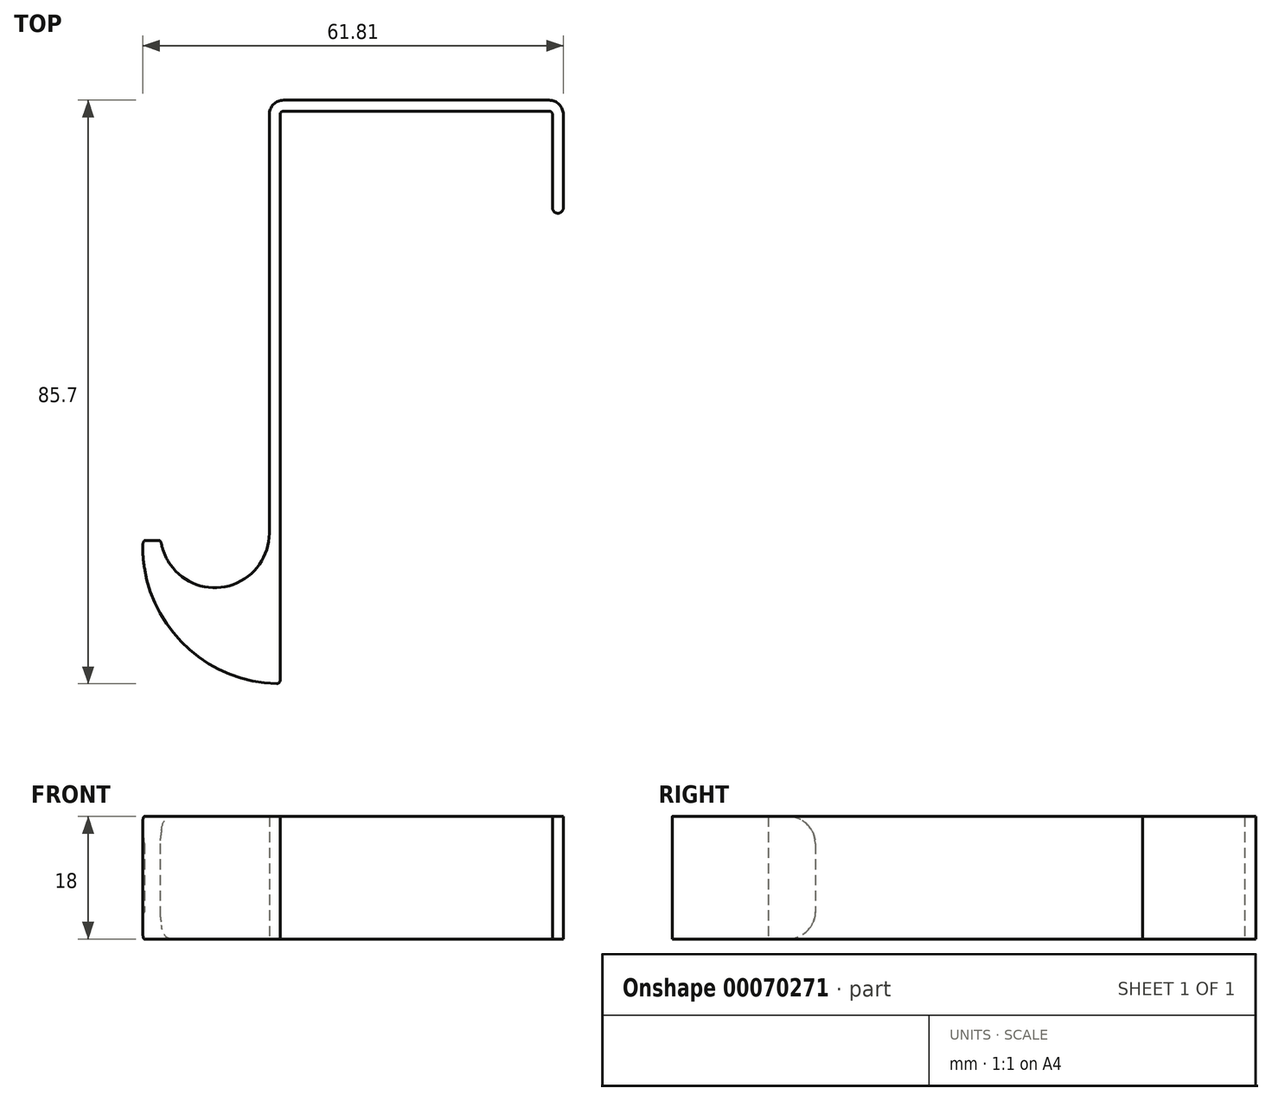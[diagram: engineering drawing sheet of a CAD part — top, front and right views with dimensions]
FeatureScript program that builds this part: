
annotation { "Feature Type Name" : "Feature", "Feature Type Description" : "" }
export const myFeature = defineFeature(function(context is Context, id is Id, definition is map)
    precondition{}
    {
        {
            var Q0;
            Q0=qCreatedBy(makeId("Top.planeOp"),FACE);
            var sketch = newSketch(context, id + "F0", { "sketchPlane" : qUnion([Q0])});
            skLineSegment(sketch, "E0", {"start": v(43.2, -15.8) * mm, "end": v(43.2, -2.1) * mm});
            skLineSegment(sketch, "E1", {"start": v(41.1, 0) * mm, "end": v(2.1, 0) * mm});
            skLineSegment(sketch, "E2", {"start": v(0, -2.1) * mm, "end": v(0, -63.6) * mm});
            skArc(sketch, "E3", {"start": v(-15.83, -65.22) * mm, "mid": v(-7.19, -71.56) * mm, "end": v(0, -63.6) * mm});
            skLineSegment(sketch, "E4", {"start": v(-15.83, -65.22) * mm, "end": v(-8, -63.6) * mm, "construction": true});
            skLineSegment(sketch, "E5", {"start": v(-8, -63.6) * mm, "end": v(0, -63.6) * mm, "construction": true});
            skArc(sketch, "E6", {"start": v(-15.83, -65.22) * mm, "mid": v(-17.35, -64.1) * mm, "end": v(-18.6, -65.5) * mm});
            skArc(sketch, "E7", {"start": v(-18.6, -65.5) * mm, "mid": v(-12.87, -79.6) * mm, "end": v(1.09, -85.7) * mm});
            skLineSegment(sketch, "E8", {"start": v(1.6, -85.2) * mm, "end": v(1.6, -2.1) * mm});
            skLineSegment(sketch, "E9", {"start": v(2.1, -1.6) * mm, "end": v(41.1, -1.6) * mm});
            skLineSegment(sketch, "E10", {"start": v(41.6, -2.1) * mm, "end": v(41.6, -15.8) * mm});
            skArc(sketch, "E11", {"start": v(41.6, -15.8) * mm, "mid": v(42.4, -16.6) * mm, "end": v(43.2, -15.8) * mm});
            skPoint(sketch, "E12.visualSharp", {"position": v(1.6, -1.6) * mm});
            skArc(sketch, "E12.filletArc", {"start": v(2.1, -1.6) * mm, "mid": v(1.75, -1.75) * mm, "end": v(1.6, -2.1) * mm});
            skPoint(sketch, "E13.visualSharp", {"position": v(41.6, -1.6) * mm});
            skArc(sketch, "E13.filletArc", {"start": v(41.6, -2.1) * mm, "mid": v(41.45, -1.75) * mm, "end": v(41.1, -1.6) * mm});
            skPoint(sketch, "E14.visualSharp", {"position": v(43.2, 0) * mm});
            skArc(sketch, "E14.filletArc", {"start": v(43.2, -2.1) * mm, "mid": v(42.58, -0.62) * mm, "end": v(41.1, 0) * mm});
            skPoint(sketch, "E15.visualSharp", {"position": v(0, 0) * mm});
            skArc(sketch, "E15.filletArc", {"start": v(2.1, 0) * mm, "mid": v(0.62, -0.62) * mm, "end": v(0, -2.1) * mm});
            skLineSegment(sketch, "E16", {"start": v(-18.6, -65.5) * mm, "end": v(-18.6, -63.6) * mm, "construction": true});
            skLineSegment(sketch, "E17", {"start": v(-18.6, -63.6) * mm, "end": v(-8, -63.6) * mm, "construction": true});
            skPoint(sketch, "E18.visualSharp", {"position": v(1.6, -85.7) * mm});
            skArc(sketch, "E18.filletArc", {"start": v(1.09, -85.7) * mm, "mid": v(1.45, -85.56) * mm, "end": v(1.6, -85.2) * mm});
            skLineSegment(sketch, "E19", {"start": v(-18.6, -64.1) * mm, "end": v(-15.83, -64.1) * mm, "construction": true});
            skLineSegment(sketch, "E20", {"start": v(-15.83, -64.1) * mm, "end": v(-15.83, -65.22) * mm, "construction": true});
            skSolve(sketch);
        }
        {
            var Q0;
            Q0=makeQuery(id+"F0.imprint","IMPRINT",FACE,{"disambiguationData":[TD([[makeQuery(id+"F0.imprint","IMPRINT",EDGE,{"derivedFrom":sQuery(id+"F0.wireOp",EDGE,"E0")}),1.0]])]});
            extrude(context, id + "F1", {"entities" : qUnion([Q0]), "endBound" : BoundingType.SYMMETRIC, "depth" : 18 * mm});
        }
        {
            var Q0;
            Q0=qCreatedBy(makeId("Right.planeOp"),FACE);
            var sketch = newSketch(context, id + "F2", { "sketchPlane" : qUnion([Q0])});
            skArc(sketch, "E21", {"start": v(-68.7, -9) * mm, "mid": v(-65.87, -7.83) * mm, "end": v(-64.7, -5) * mm});
            skLineSegment(sketch, "E22", {"start": v(-64.7, -5) * mm, "end": v(-64.7, 5) * mm});
            skArc(sketch, "E23", {"start": v(-64.7, 5) * mm, "mid": v(-65.87, 7.83) * mm, "end": v(-68.7, 9) * mm});
            skLineSegment(sketch, "E24", {"start": v(-68.7, -9) * mm, "end": v(-68.7, -10) * mm});
            skLineSegment(sketch, "E25", {"start": v(-68.7, -10) * mm, "end": v(-63.7, -10) * mm});
            skLineSegment(sketch, "E26", {"start": v(-63.7, -10) * mm, "end": v(-63.7, 10) * mm});
            skLineSegment(sketch, "E27", {"start": v(-63.7, 10) * mm, "end": v(-68.7, 10) * mm});
            skLineSegment(sketch, "E28", {"start": v(-68.7, 10) * mm, "end": v(-68.7, 9) * mm});
            skLineSegment(sketch, "E29", {"start": v(-68.7, -9) * mm, "end": v(-68.7, 9) * mm, "construction": true});
            skLineSegment(sketch, "E30", {"start": v(-63.7, 0) * mm, "end": v(-68.7, 0) * mm, "construction": true});
            skSolve(sketch);
        }
        {
            var Q0;
            Q0=qSketchRegion(id+"F2",true);
            extrude(context, id + "F3", {"entities" : qUnion([Q0]), "operationType" : NewBodyOperationType.REMOVE, "oppositeDirection" : true, "depth" : 30 * mm, "hasSecondDirection" : true, "secondDirectionOppositeDirection" : true, "secondDirectionDepth" : 10 * mm});
        }
    });
